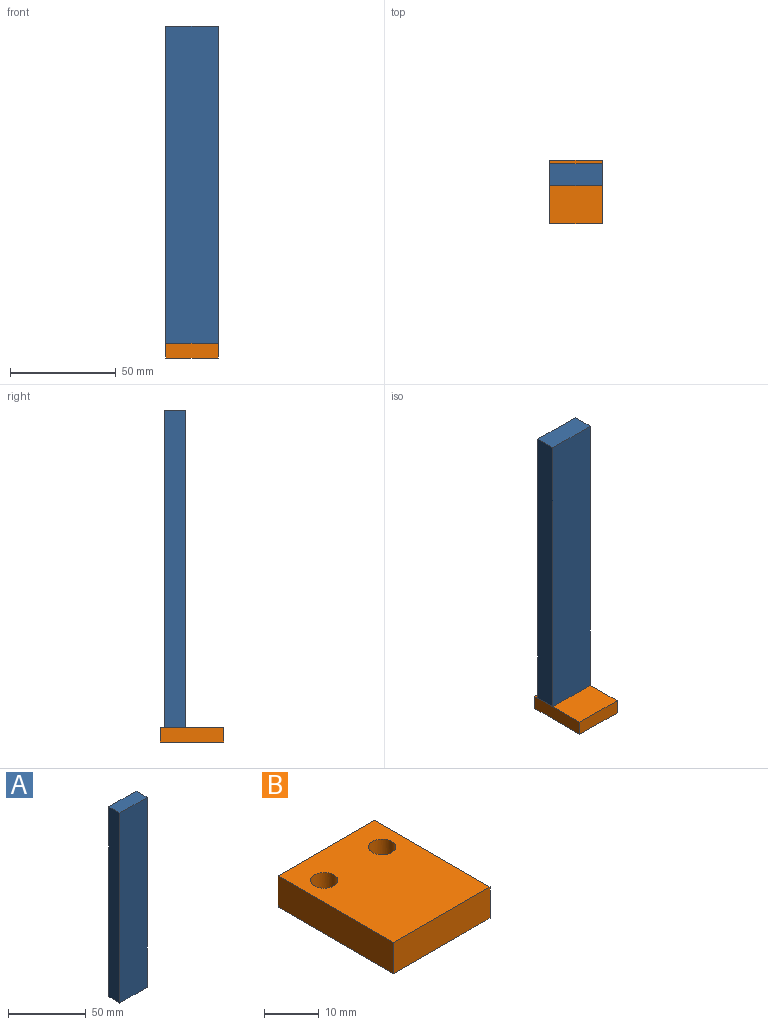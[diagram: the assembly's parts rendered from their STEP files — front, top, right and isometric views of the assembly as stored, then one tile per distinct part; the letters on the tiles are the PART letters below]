
ASSEMBLY  parts=2 mates=1
PART A: 10 faces, bbox 25x10x150 mm
  f0: plane 150x25mm, normal (0,1,0), area 3750mm2, adj f1,f3,f4,f5
  f1: plane 150x10mm, normal (-1,0,0), area 1500mm2, adj f0,f2,f4,f5
  f2: plane 150x25mm, normal (0,-1,0), area 3750mm2, adj f1,f3,f4,f5
  f3: plane 150x10mm, normal (1,0,0), area 1500mm2, adj f0,f2,f4,f5
  f4: plane 25x10mm, normal (0,0,1), area 250mm2, adj f0,f1,f2,f3
  f5: plane 25x10mm, normal (0,0,-1), area 235.9mm2, adj f0,f1,f2,f3,f6,f8
  f6: cylinder r=1.5mm len=20mm, axis (0,0,-1), area 188.5mm2, adj f5,f7
  f7: plane 3x3mm, normal (0,0,-1), area 7.1mm2, adj f6
  f8: cylinder r=1.5mm len=20mm, axis (0,0,-1), area 188.5mm2, adj f5,f9
  f9: plane 3x3mm, normal (0,0,-1), area 7.1mm2, adj f8
PART B: 12 faces, bbox 25x30x7 mm
  f0: plane 30x7mm, normal (-1,0,0), area 210mm2, adj f1,f3,f4,f5
  f1: plane 25x7mm, normal (0,-1,0), area 175mm2, adj f0,f2,f4,f5
  f2: plane 30x7mm, normal (1,0,0), area 210mm2, adj f1,f3,f4,f5
  f3: plane 25x7mm, normal (0,1,0), area 175mm2, adj f0,f2,f4,f5
  f4: plane 30x25mm, normal (0,0,1), area 710.7mm2, adj f0,f1,f2,f3,f6,f9
  f5: plane 30x25mm, normal (0,0,-1), area 622.8mm2, adj f0,f1,f2,f3,f8,f11
  f6: cylinder r=2.5mm len=5mm, axis (0,0,-1), area 55mm2, adj f4,f7
  f7: plane 9x9mm, normal (0,0,-1), area 44mm2, adj f6,f8
  f8: cylinder r=4.5mm len=9mm, axis (0,0,-1), area 99mm2, adj f5,f7
  f9: cylinder r=2.5mm len=5mm, axis (0,0,-1), area 55mm2, adj f4,f10
  f10: plane 9x9mm, normal (0,0,-1), area 44mm2, adj f9,f11
  f11: cylinder r=4.5mm len=9mm, axis (0,0,-1), area 99mm2, adj f5,f10
PLACE A t=(-33.03,-12.05,15.54)mm
PLACE B t=(-33.03,-40.05,8.54)mm
MATE fastened B.f6 <-> A.f8  axis (0,0,1) through (-28.03,-17.05,15.54)mm
